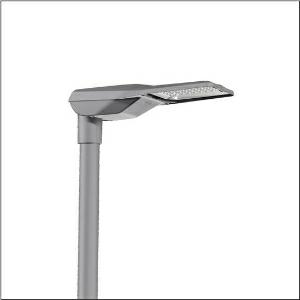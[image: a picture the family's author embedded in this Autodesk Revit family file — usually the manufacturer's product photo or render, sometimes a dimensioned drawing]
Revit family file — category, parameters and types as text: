
# Revit family: streetlight_sl_21_iq_mini___p0_8ab_5xe2r31d08gb_0de2
name_source: partatom
category: Lighting Fixtures
units: mm (PartAtom-declared; Revit-internal decimal feet)

## family parameters
Cut with Voids When Loaded = No
Host = Face
Light Source = No
Part Type = Normal
Room Calculation Point = No
Round Connector Dimension = Use Diameter
Shared = No

## types (1)
- --- (1 x LED, 4930 lm, 37.1 W, 3000K)
    Apparent Load = 37 VA
    CIE Flux Codes = 36 71 98 100 100
    Color Rendering = 70
    Color Temperature = 3000K
    Default Elevation = 1800 mm
    Description = Streetlight SL 21 iQ mini, mast luminaire, primary light control with lens, of PMMA, primary optical cover: cover, of toughened safety glass, transparent, light distribution: P0.8aB, light emission: direct distribution, primary light characteristic: asymmetric, installation type: post-top, side-entry, LED, High Power LED, rated luminous flux: 4.930lm, luminous efficacy: 133lm/W, light colour: 730, colour temperature: 3000K, control gear: iQ-Comfort, control: pre-setting: linear dimming characteristic, Auto-Match, Temp-Guard, Lumen-Switch, Night-Set, Smart-Wire, Light-Fading, Desk-Remote (wireless, voltage-free reading and setting of iQ features in the workshop via application-optimized NFC function/RFID function), optimised constant luminous flux control (CLO 2.0), mains connection: 220..240V, AC, 50/60Hz, start of lifetime: 37W, end of service life: 39W, reduction: 18W, luminaire housing, of diecast aluminium, powder-coated, Siteco® metallic grey (DB 702S), corrosivity category C5 mid according to DIN EN ISO 12944, please order mast flange separately, inclination adjustable: 0°, 5°, 10°, 15°, sealing non-destructively replaceable, multi-level sealing system, length: 628mm, width: 235mm, height: 110mm, mast flange for spigot size: 42mm (side-entry): 5XC10008XM4, 60/48mm (side-entry/post-top): 5XC10108XM2, 76/60mm (side-entry/post-top): 5XC10108XM1, mounting height: 4..8m, protection rating (complete): IP66, insulation class (complete): insulation class II (safety insulation), certification: CE, ENEC, ENEC+, VDE, impact resistance: IK09, permissible operating ambient temperature for outdoor applications: -40..+50°C, standard-compliant lighting for roads and squares, packaging unit: 1 piece

Light Distribution: P0.8aB
    Height = 110 mm
    Lamp = 1 x LED
    Lamp Light Flux = 4930 lm
    Lamp Power = 37.1 W
    Lamp count = 1
    Length = 625 mm
    Luminous efficacy = 133 lm/W
    Manufacturer = Siteco
    ModVariant = No
    Model = 5XE2R31D08GB
    Number of Poles = 1
    OnlyDefault = Yes
    Power Factor = 1
    Product Name = Streetlight SL 21 iQ mini | P0.8aB
    Product group = mast luminaire | pylon top
    ProductGroupID = 6100
    Protection Class = Protection class II
    Protection Degree = IP 66
    RLX_Detail_Level = 1
    RLX_Emergency_Light_Flux = 0 lm
    RLX_Emergency_Type = 0
    RLX_Emergency_Type_DB = No
    RlxData = <blob elided: 92157 chars, md5=71f848be>
    Socket = socket
    Standby Power = 0 W
    System Light Flux = 4930 lm
    System Power = 37 W
    Type Comments = factory setting: luminous flux: 100 % | dim-lin: 254 | 385 mA
    Type Image = l_1003519.jpg
    URL = http://relux.com
    VarID = @adj_071566
    Voltage = 0 V
    Weight = 0.00 kg
    Width = 234 mm

## geometry (parser evidence)
native form markers: Blend x4, Sweep x11
no freeform markers — native parametric forms only
